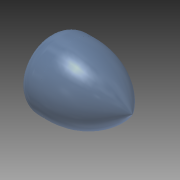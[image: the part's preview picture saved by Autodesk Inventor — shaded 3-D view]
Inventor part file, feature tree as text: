
AUTODESK INVENTOR PART (.ipt)
format: ipt  version: 2015 (Build 190159000, 159)  size: 145,920 bytes
history: native  units: mm
features: sketch x2, other x1, revolve x1, extrude x1, fillet x1
ambient origin geometry x8: Origin, YZ Plane, XZ Plane, XY Plane, X Axis, Y Axis, Z Axis, Center Point
bodies: Body1 (feature_tree)
feature tree (6):
  other  "Sólido1"
  revolve  "Revolución1"  [1 undecoded]
  extrude  "Extrusión2"  [1 undecoded]
  fillet  "Empalme3"  [1 undecoded]
  sketch  "Boceto1"  dims[d0=20.0mm d1=45.0mm d2=20.0mm d3=100.0mm d4=90.0deg d5=20.0mm d6=135.0mm d7=3.0mm d8=90.0deg d13=10.0mm d14=0.0mm]
  sketch  "Boceto3"  dims[d15=20.0mm]
note: 3 required parameter values undecoded (feature->parameter linkage not recoverable at this tier; creation-order binding heuristic only, values carry confidence <= 0.55)